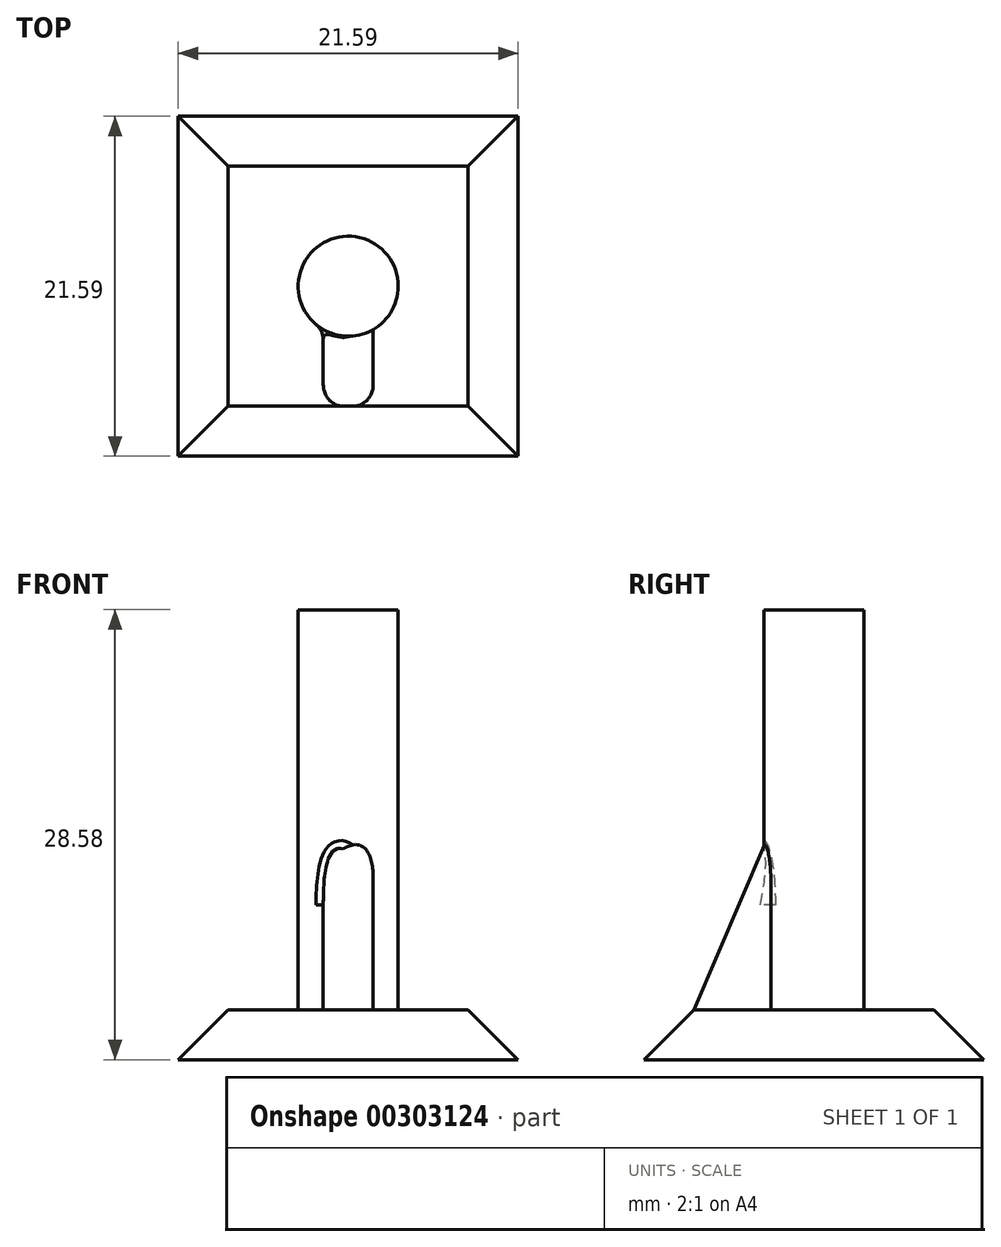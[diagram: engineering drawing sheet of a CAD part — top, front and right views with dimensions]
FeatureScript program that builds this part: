
annotation { "Feature Type Name" : "Feature", "Feature Type Description" : "" }
export const myFeature = defineFeature(function(context is Context, id is Id, definition is map)
    precondition{}
    {
        {
            var Q0;
            Q0=qCreatedBy(makeId("Top.planeOp"),FACE);
            var sketch = newSketch(context, id + "F0", { "sketchPlane" : qUnion([Q0])});
            skLineSegment(sketch, "E0.bottom", {"start": v(0, 0) * mm, "end": v(25.4, 0) * mm});
            skLineSegment(sketch, "E0.top", {"start": v(0, 25.4) * mm, "end": v(25.4, 25.4) * mm});
            skLineSegment(sketch, "E0.left", {"start": v(0, 0) * mm, "end": v(0, 25.4) * mm});
            skLineSegment(sketch, "E0.right", {"start": v(25.4, 0) * mm, "end": v(25.4, 25.4) * mm});
            skSolve(sketch);
        }
        {
            var Q0;
            Q0 = qSketchRegion(id + "F0", true);
            extrude(context, id + "F1", {"entities" : qUnion([Q0]), "depth" : 3.17 * mm});
        }
        {
            var Q0;
            Q0=makeQuery(id+"F1.opExtrude","CAP_EDGE",EDGE,{"disambiguationData":[OSD([sQuery(id+"F0.wireOp",EDGE,"E0.bottom")])],"isStart":false});
            var Q1;
            Q1=makeQuery(id+"F1.opExtrude","CAP_EDGE",EDGE,{"disambiguationData":[OSD([sQuery(id+"F0.wireOp",EDGE,"E0.right")])],"isStart":false});
            var Q2;
            Q2=makeQuery(id+"F1.opExtrude","CAP_EDGE",EDGE,{"disambiguationData":[OSD([sQuery(id+"F0.wireOp",EDGE,"E0.top")])],"isStart":false});
            var Q3;
            Q3=makeQuery(id+"F1.opExtrude","CAP_EDGE",EDGE,{"disambiguationData":[OSD([sQuery(id+"F0.wireOp",EDGE,"E0.left")])],"isStart":false});
            chamfer(context, id + "F2", {"entities" : qUnion([Q0, Q1, Q2, Q3]), "width" : 5.08 * mm, "tangentPropagation" : true});
        }
        {
            var Q0;
            Q0=makeQuery(id+"F1.opExtrude","CAP_FACE",FACE,{"disambiguationData":[OSD([sQuery(id+"F0.wireOp",EDGE,"E0.bottom"),sQuery(id+"F0.wireOp",EDGE,"E0.top"),sQuery(id+"F0.wireOp",EDGE,"E0.left"),sQuery(id+"F0.wireOp",EDGE,"E0.right")])],"isStart":false});
            var sketch = newSketch(context, id + "F3", { "sketchPlane" : qUnion([Q0])});
            skCircle(sketch, "E1", {"center": v(12.7, 12.7) * mm, "radius": 3.18 * mm});
            skPoint(sketch, "E1.centerSnap0", {"position": v(20.32, 12.7) * mm});
            skPoint(sketch, "E1.centerSnap1", {"position": v(12.7, 20.32) * mm});
            skSolve(sketch);
        }
        {
            var Q0;
            Q0 = qSketchRegion(id + "F3", true);
            extrude(context, id + "F4", {"entities" : qUnion([Q0]), "operationType" : NewBodyOperationType.ADD, "depth" : 25.4 * mm});
        }
        {
            var Q0;
            Q0=makeQuery(id+"F1.opExtrude","CAP_FACE",FACE,{"disambiguationData":[OSD([sQuery(id+"F0.wireOp",EDGE,"E0.bottom"),sQuery(id+"F0.wireOp",EDGE,"E0.top"),sQuery(id+"F0.wireOp",EDGE,"E0.left"),sQuery(id+"F0.wireOp",EDGE,"E0.right")])],"isStart":false});
            var sketch = newSketch(context, id + "F5", { "sketchPlane" : qUnion([Q0])});
            skLineSegment(sketch, "E2", {"start": v(12.7, 20.32) * mm, "end": v(12.7, 5.08) * mm});
            skSolve(sketch);
        }
        {
            var Q0;
            Q0=sQuery(id+"F5.wireOp",EDGE,"E2");
            cPlane(context, id + "F6", {"entities" : qUnion([Q0]), "cplaneType" : CPlaneType.LINE_ANGLE, "offset" : 25.4 * mm, "angle" : 90 * degree, "width" : 152.4 * mm, "height" : 152.4 * mm});
        }
        {
            var Q0;
            Q0=qCreatedBy(id+"F6.planeOp",FACE);
            var sketch = newSketch(context, id + "F7", { "sketchPlane" : qUnion([Q0])});
            skLineSegment(sketch, "E3", {"start": v(5.08, 3.17) * mm, "end": v(11.45, 18.13) * mm});
            skLineSegment(sketch, "E4", {"start": v(11.45, 18.13) * mm, "end": v(11.45, 1.96) * mm});
            skLineSegment(sketch, "E5", {"start": v(11.45, 1.96) * mm, "end": v(5.1, 1.96) * mm});
            skLineSegment(sketch, "E6", {"start": v(5.08, 3.18) * mm, "end": v(5.1, 1.96) * mm});
            skSolve(sketch);
        }
        {
            var Q0;
            Q0 = qSketchRegion(id + "F7", true);
            extrude(context, id + "F8", {"entities" : qUnion([Q0]), "operationType" : NewBodyOperationType.ADD, "endBound" : BoundingType.SYMMETRIC, "depth" : 3.17 * mm});
        }
        {
            var Q0;
            Q0=makeQuery(id+"F8.opExtrude","CAP_EDGE",EDGE,{"disambiguationData":[OSD([sQuery(id+"F7.wireOp",EDGE,"E3")])],"isStart":false});
            var Q1;
            Q1=makeQuery(id+"F8.opExtrude","CAP_EDGE",EDGE,{"disambiguationData":[OSD([sQuery(id+"F7.wireOp",EDGE,"E3")])],"isStart":true});
            var Q2;
            Q2=makeQuery(id+"F8.boolean.opBoolean","INTERSECT",EDGE,{"derivedFrom":[makeQuery(id+"F4.opExtrude","SWEPT_FACE",FACE,{"disambiguationData":[OSD([sQuery(id+"F3.wireOp",EDGE,"E1")])]}),makeQuery(id+"F8.opExtrude","CAP_FACE",FACE,{"disambiguationData":[OSD([sQuery(id+"F7.wireOp",EDGE,"E3"),sQuery(id+"F7.wireOp",EDGE,"E4"),sQuery(id+"F7.wireOp",EDGE,"E5"),sQuery(id+"F7.wireOp",EDGE,"E6")])],"isStart":true})]});
            var Q3;
            Q3=makeQuery(id+"F4.opExtrude","CAP_EDGE",EDGE,{"disambiguationData":[OSD([sQuery(id+"F3.wireOp",EDGE,"E1")])],"isStart":true});
            fillet(context, id + "F9", {"entities" : qUnion([Q0, Q1, Q2, Q3]), "radius" : 1.27 * mm, "tangentPropagation" : true, "allowEdgeOverflow" : false});
        }
    });
